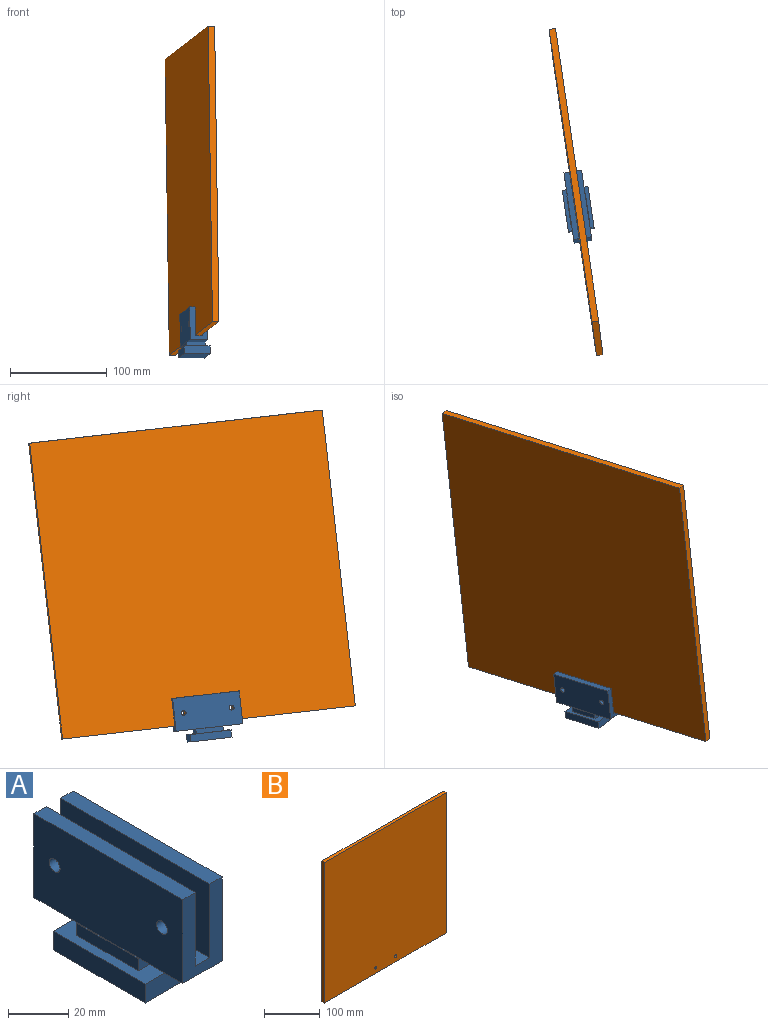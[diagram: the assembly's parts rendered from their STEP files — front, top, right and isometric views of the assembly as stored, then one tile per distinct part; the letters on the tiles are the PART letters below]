
ASSEMBLY  parts=2 mates=1
PART A: 27 faces, bbox 26.8x70.1x46.8 mm
  f0: plane 20.57x18.49mm, normal (0,0,-1), area 380.4mm2, adj f4,f6,f9,f20
  f1: plane 70.13x30mm, normal (-1,0,0), area 2063.2mm2, adj f2,f5,f6,f7,f17,f18
  f2: plane 70.13x6.81mm, normal (0,0,1), area 477.4mm2, adj f1,f6,f7,f19
  f3: plane 20.57x18.49mm, normal (0,0,-1), area 380.4mm2, adj f4,f7,f10,f20
  f4: plane 70.13x34.19mm, normal (1,0,0), area 2357.1mm2, adj f0,f3,f5,f6,f7,f8,f17,f18
  f5: plane 70.13x5.84mm, normal (0,0,1), area 409.7mm2, adj f1,f4,f6,f7
  f6: plane 34.19x18.49mm, normal (0,-1,0), area 428mm2, adj f0,f1,f2,f4,f5,f19,f20,f21
  f7: plane 34.19x18.49mm, normal (0,1,0), area 428mm2, adj f1,f2,f3,f4,f5,f19,f20,f21
  f8: plane 28.98x0.41mm, normal (0,0,1), area 11.8mm2, adj f4,f9,f10,f11
  f9: plane 19.3x4.93mm, normal (0,-1,0), area 95.1mm2, adj f0,f8,f11,f12,f22,f23
  f10: plane 19.3x4.93mm, normal (0,1,0), area 95.1mm2, adj f3,f8,f11,f12,f22,f23
  f11: plane 28.98x4.93mm, normal (1,0,0), area 142.8mm2, adj f8,f9,f10,f12
  f12: plane 43.23x26.82mm, normal (0,0,1), area 600.1mm2, adj f9,f10,f11,f13,f15,f16,f23,f24
  f13: plane 26.82x7.67mm, normal (0,-1,0), area 205.7mm2, adj f12,f14,f16,f24
  f14: plane 43.23x26.82mm, normal (0,0,-1), area 1159.6mm2, adj f13,f15,f16,f24
  f15: plane 26.82x7.67mm, normal (0,1,0), area 205.7mm2, adj f12,f14,f16,f24
  f16: plane 43.23x7.67mm, normal (1,0,0), area 331.6mm2, adj f12,f13,f14,f15
  f17: cylinder r=2.54mm len=5.84mm, axis (1,0,0), area 93.2mm2, adj f1,f4
  f18: cylinder r=2.54mm len=5.84mm, axis (1,0,0), area 93.2mm2, adj f1,f4
  f19: plane 70.13x30mm, normal (1,0,0), area 2063.2mm2, adj f2,f6,f7,f21,f25,f26
  f20: plane 70.13x34.19mm, normal (-1,0,0), area 2357.1mm2, adj f0,f3,f6,f7,f21,f22,f25,f26
  f21: plane 70.13x5.84mm, normal (0,0,1), area 409.7mm2, adj f6,f7,f19,f20
  f22: plane 28.98x0.41mm, normal (0,0,1), area 11.8mm2, adj f9,f10,f20,f23
  f23: plane 28.98x4.93mm, normal (-1,0,0), area 142.8mm2, adj f9,f10,f12,f22
  f24: plane 43.23x7.67mm, normal (-1,0,0), area 331.6mm2, adj f12,f13,f14,f15
  f25: cylinder r=2.54mm len=5.84mm, axis (-1,0,0), area 93.2mm2, adj f19,f20
  f26: cylinder r=2.54mm len=5.84mm, axis (-1,0,0), area 93.2mm2, adj f19,f20
PART B: 8 faces, bbox 308x6.8x308 mm
  f0: plane 307.98x6.78mm, normal (0,0,1), area 2088.6mm2, adj f1,f3,f4,f5
  f1: plane 307.98x6.78mm, normal (-1,0,0), area 2088.6mm2, adj f0,f2,f4,f5
  f2: plane 307.98x6.78mm, normal (0,0,-1), area 2088.6mm2, adj f1,f3,f4,f5
  f3: plane 307.98x6.78mm, normal (1,0,0), area 2088.6mm2, adj f0,f2,f4,f5
  f4: plane 307.98x307.98mm, normal (0,-1,0), area 94808.1mm2, adj f0,f1,f2,f3,f6,f7
  f5: plane 307.98x307.98mm, normal (0,1,0), area 94808.1mm2, adj f0,f1,f2,f3,f6,f7
  f6: cylinder r=2.54mm len=6.78mm, axis (0,-1,0), area 108.2mm2, adj f4,f5
  f7: cylinder r=2.54mm len=6.78mm, axis (0,-1,0), area 108.2mm2, adj f4,f5
PLACE A rot(axis=(-0.61,-0.03,0.79),10.5deg) t=(28.61,7.48,-63.06)mm
PLACE B rot(axis=(-0.06,0.05,1),98.5deg) t=(24.39,14.29,55.74)mm
MATE fastened A.f25 <-> B.f6  axis (0.99,0.15,0) through (21.46,32.75,-57.76)mm
